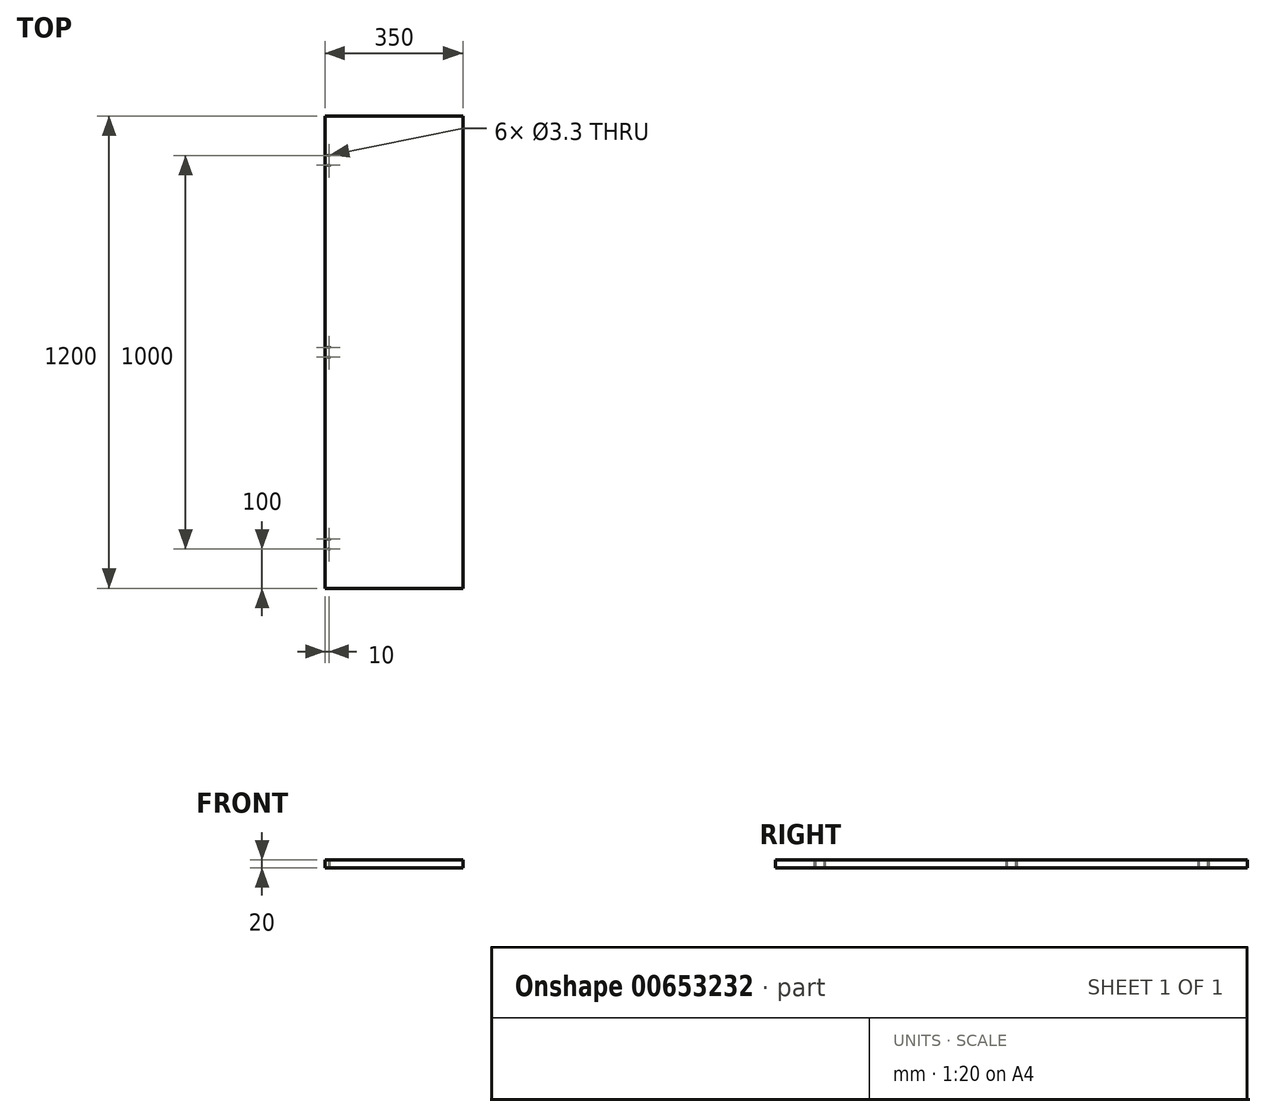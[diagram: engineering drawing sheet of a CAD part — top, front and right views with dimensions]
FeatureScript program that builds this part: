
annotation { "Feature Type Name" : "Feature", "Feature Type Description" : "" }
export const myFeature = defineFeature(function(context is Context, id is Id, definition is map)
    precondition{}
    {
        {
            var Q0;
            Q0=qCreatedBy(makeId("Top.planeOp"),FACE);
            var sketch = newSketch(context, id + "F0", { "sketchPlane" : qUnion([Q0])});
            skLineSegment(sketch, "E0.bottom", {"start": v(175, 600) * mm, "end": v(-175, 600) * mm});
            skLineSegment(sketch, "E0.top", {"start": v(175, -600) * mm, "end": v(-175, -600) * mm});
            skLineSegment(sketch, "E0.left", {"start": v(175, 600) * mm, "end": v(175, -600) * mm});
            skLineSegment(sketch, "E0.right", {"start": v(-175, 600) * mm, "end": v(-175, -600) * mm});
            skPoint(sketch, "E0.middle", {"position": v(0, 0) * mm});
            skSolve(sketch);
        }
        {
            var Q0;
            Q0=makeQuery(id+"F0.imprint","IMPRINT",FACE,{"disambiguationData":[TD([[makeQuery(id+"F0.imprint","IMPRINT",EDGE,{"derivedFrom":sQuery(id+"F0.wireOp",EDGE,"E0.bottom")}),1.0]])]});
            extrude(context, id + "F1", {"entities" : qUnion([Q0]), "depth" : 20 * mm, "offsetDistance" : 25 * mm});
        }
        {
            var Q0;
            Q0=makeQuery(id+"F1.opExtrude","CAP_FACE",FACE,{"disambiguationData":[OSD([sQuery(id+"F0.wireOp",EDGE,"E0.bottom"),sQuery(id+"F0.wireOp",EDGE,"E0.top"),sQuery(id+"F0.wireOp",EDGE,"E0.left"),sQuery(id+"F0.wireOp",EDGE,"E0.right")])],"isStart":true});
            var sketch = newSketch(context, id + "F2", { "sketchPlane" : qUnion([Q0])});
            skLineSegment(sketch, "E1", {"start": v(-165, 600) * mm, "end": v(-165, -600) * mm, "construction": true});
            skPoint(sketch, "E2", {"position": v(-165, 500) * mm});
            skPoint(sketch, "E3", {"position": v(-165, 475) * mm});
            skPoint(sketch, "E4", {"position": v(-165, 12.5) * mm});
            skPoint(sketch, "E5", {"position": v(-165, -12.5) * mm});
            skPoint(sketch, "E6", {"position": v(-165, -475) * mm});
            skPoint(sketch, "E7", {"position": v(-165, -500) * mm});
            skSolve(sketch);
        }
        {
            var Q0;
            Q0=sQuery(id+"F2.wireOp",VERTEX,"E2");
            var Q1;
            Q1=sQuery(id+"F2.wireOp",VERTEX,"E3");
            var Q2;
            Q2=sQuery(id+"F2.wireOp",VERTEX,"E4");
            var Q3;
            Q3=sQuery(id+"F2.wireOp",VERTEX,"E5");
            var Q4;
            Q4=sQuery(id+"F2.wireOp",VERTEX,"E7");
            var Q5;
            Q5=sQuery(id+"F2.wireOp",VERTEX,"E6");
            var Q6;
            Q6=makeQuery(id+"F1.opExtrude","SWEPT_BODY",BODY,{"disambiguationData":[OSD([sQuery(id+"F0.wireOp",EDGE,"E0.bottom"),sQuery(id+"F0.wireOp",EDGE,"E0.top"),sQuery(id+"F0.wireOp",EDGE,"E0.left"),sQuery(id+"F0.wireOp",EDGE,"E0.right")])]});
            hole(context, id + "F3", {"style" : HoleStyle.SIMPLE, "endStyle" : HoleEndStyle.THROUGH, "standardTappedOrClearance" : lookupTablePath({ "standard" : "ISO", "engagement" : "75%", "pitch" : "0.7 mm", "size" : "M4", "type" : "Tapped" }), "standardBlindInLast" : lookupTablePath({ "standard" : "ISO", "engagement" : "75%", "pitch" : "0.7 mm", "size" : "M4", "type" : "Tapped" }), "holeDiameter" : 3.3 * mm, "majorDiameter" : 4 * mm, "showTappedDepth" : true, "isTappedThrough" : true, "tappedDepth" : 12 * mm, "tapClearance" : 3, "startFromSketch" : true, "locations" : qUnion([Q0, Q1, Q2, Q3, Q4, Q5]), "scope" : qUnion([Q6])});
        }
    });
